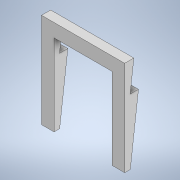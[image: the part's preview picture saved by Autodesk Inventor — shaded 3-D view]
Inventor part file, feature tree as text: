
AUTODESK INVENTOR PART (.ipt)
format: ipt  version: 2022.1 (Build 261234020, 234B)  size: 697,856 bytes
history: native  units: in
note: dims shown in document units (in); Inventor stores cm internally (conversion verified against a paired STEP export)
features: sketch x3, extrude x2, emboss x1
ambient origin geometry x8: Origin, YZ Plane, XZ Plane, XY Plane, X Axis, Y Axis, Z Axis, Center Point
bodies: Body1 (feature_tree)
feature tree (6):
  extrude  "Extrusion6"  Depth=4.0in
  extrude  "Extrusion7"  Depth=0.5in
  emboss  "Emboss1"
  sketch  "Sketch4"  dims[d28=0.5in d29=4.0in]
  sketch  "Sketch6"  dims[d30=4.0in d31=0.5in]
  sketch  "Sketch7"  dims[d32=4.0in d33=5.7in d34=0.55in d35=1.77in d57=5.0in d58=0.0in d59=4.9in d60=1.75in d61=0.0in d62=0.0in d63=0.1in d64=0.0in d65=0.5in]
